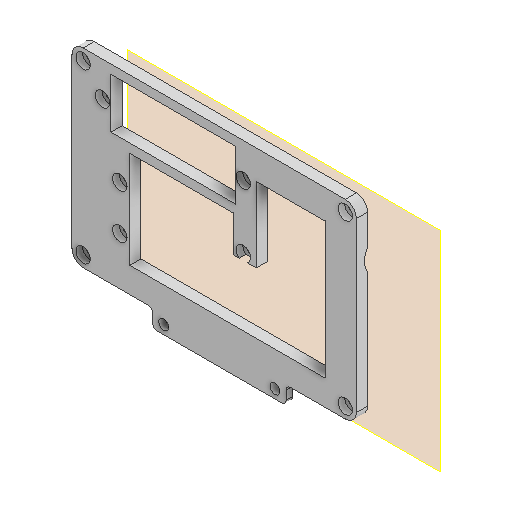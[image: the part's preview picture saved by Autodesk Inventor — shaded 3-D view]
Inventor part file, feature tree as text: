
AUTODESK INVENTOR PART (.ipt)
format: ipt  version: 2025.3 (Build 293356000, 356)  size: 268,288 bytes
history: native  units: mm
features: reference x8, other x6, extrude x5, sketch x3, plane x2, fillet x1, hole x1, projected_geometry x1
ambient origin geometry x8: Origin, YZ Plane, XZ Plane, XY Plane, X Axis, Y Axis, Z Axis, Center Point
bodies: Volumenkörper1 (feature_tree)
feature tree (27):
  plane  "Arbeitsebene1"
  extrude  "Extrusion1"  Depth=2.8mm
  extrude  "Extrusion2"  Depth=5.0mm
  fillet  "Rundung1"  Radius=5.0mm
  hole  "Bohrung1"  [1 undecoded]
  plane  "Arbeitsebene2"
  extrude  "Extrusion3"  Depth=20.0mm
  extrude  "Extrusion4"  Depth=20.0mm
  extrude  "Extrusion5"  Depth=5.0mm
  reference  "Referenz1"
  sketch  "Skizze2"  dims[d0=2.8mm d1=2.8mm]
  sketch  "Skizze3"  dims[d2=2.8mm d3=2.8mm d4=5.0mm d5=0.0mm]
  projected_geometry  "Projizierte Kontur1"
  reference  "Referenz2"
  reference  "Referenz3"
  reference  "Referenz4"
  sketch  "Skizze5"  dims[d6=60.0mm d7=8.0mm d8=4.5mm d9=4.5mm d10=5.0mm d11=50.0mm d12=3.0mm d13=0.0mm d14=2.0mm d15=2.9mm d16=6.0mm d17=6.5mm d18=3.0mm d19=90.0deg d20=8.0mm d21=20.594885mm d22=20.0mm d23=20.0mm d24=1.5mm d25=0.0mm d26=0.0mm d27=10.0mm d28=0.0mm d29=4.0mm d30=17.0mm d31=20.0mm d32=0.0mm]
  reference  "Referenz5"
  reference  "Referenz6"
  reference  "Referenz7"
  reference  "Referenz8"
  other  "Assembly_Guinardia_V3.iam"
  other  "10_Wellplate_base_v2:1"
  other  "<userpath>\Documents\HoLiSheet\INVENTOR\Assembly_HoliSheet_v6.iam"
  other  "Assembly_HoliSheet_v6.iam"
  other  "10_Wellplate_base_v6:1"
  other  "Assembly_Guinardia_V2.iam"
note: 1 required parameter value undecoded (feature->parameter linkage not recoverable at this tier; creation-order binding heuristic only, values carry confidence <= 0.55)
